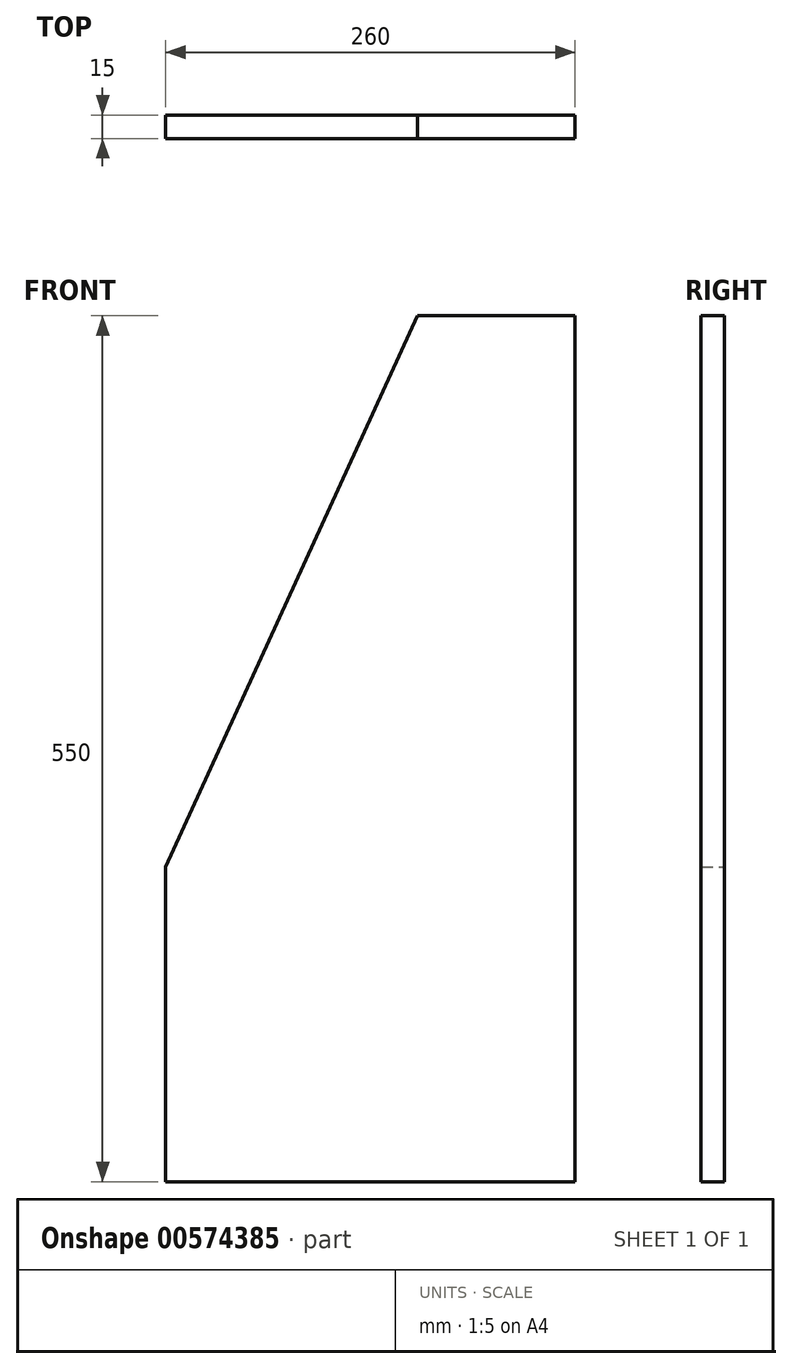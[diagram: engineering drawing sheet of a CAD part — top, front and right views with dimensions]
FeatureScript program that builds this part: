
annotation { "Feature Type Name" : "Feature", "Feature Type Description" : "" }
export const myFeature = defineFeature(function(context is Context, id is Id, definition is map)
    precondition{}
    {
        {
            var Q0;
            Q0=qCreatedBy(makeId("Front.planeOp"),FACE);
            var sketch = newSketch(context, id + "F0", { "sketchPlane" : qUnion([Q0])});
            skLineSegment(sketch, "E0", {"start": v(130, 350) * mm, "end": v(130, -200) * mm});
            skLineSegment(sketch, "E1", {"start": v(130, -200) * mm, "end": v(-130, -200) * mm});
            skLineSegment(sketch, "E2", {"start": v(-130, -200) * mm, "end": v(-130, 0) * mm});
            skLineSegment(sketch, "E3", {"start": v(-130, 0) * mm, "end": v(30, 350) * mm});
            skLineSegment(sketch, "E4", {"start": v(30, 350) * mm, "end": v(130, 350) * mm});
            skSolve(sketch);
        }
        {
            var Q0;
            Q0=makeQuery(id+"F0.imprint","IMPRINT",FACE,{"disambiguationData":[TD([[makeQuery(id+"F0.imprint","IMPRINT",EDGE,{"derivedFrom":sQuery(id+"F0.wireOp",EDGE,"E0")}),-1.0]])]});
            extrude(context, id + "F1", {"entities" : qUnion([Q0]), "depth" : 15 * mm, "offsetDistance" : 25 * mm});
        }
    });
